# Revit family: ON2.5UM-NRG_5BF
name_source: partatom
category: Mechanical Equipment
units: mm (PartAtom-declared; Revit-internal decimal feet)

## family parameters
Always vertical = Yes
Cut with Voids When Loaded = No
OmniClass Number = 23.40.40.11.17
OmniClass Title = Refrigerated Cases
Part Type = Normal
Room Calculation Point = No
Round Connector Dimension = Use Radius
Shared = No
Work Plane-Based = Yes

## types (32) — shared parameters
11" BF = Yes
ANTI SWEAT HEATER AMPS = 0 A
BASE HEIGHT = 5 1/8"
BTU PER FOOT CONVENTIONAL = 797
BTU PER FOOT PARALLEL = 739
CERTIFICATIONS = NSF 7, UL471, CSA
COIL REFRIGERATION CHARGE = 0.00 lb
CONTROL TYPE = T-STAT
DATE = 10/03/12
DEDICATED CIRCUIT = YES
DEFROST PHASE = 1
DEFROST TIME AND DURATION = 2 @ 60 MIN
DEFROST WATTAGE = 0 W
DIEBOARD HEIGHT = 0"
DISCHARGE AIR TEMPERATURE = 28 °F
DRAIN LINE CONNECTION = Drain Connection
DRAIN LINE DIAMETER = 2"
DRAIN LINE RADIUS = 1"
DRAIN PIPE TYPE = PVC
DRIP PAN PLUMB TYPE = HARD
Default Elevation = 48"
Description = NARROW MULTI DECK MERCHANDISER
Discharge Air Velocity (FPM) = 250 FPM
ELECTRIC DEFROST = No
ELECTRICAL DEFROST VOLTAGE = 0 V
EVAPORATOR TEMPERATURE = 22 °F
FAN AMPS = 0 A
FAN CONNECTOR DESCRIPTION = FAN AND ANTI SWEAT CONNECTOR
FAN NUMBER OF POLES = 1
FAN TYPE = ECM
GROUND FAULT PROTECTION = NO
HOT GAS DEFROST = No
High Efficiency Amps = 0 A
High Power (Cornice) Amps = 0 A
ISOLATED GROUND REQUIRED = NO
Keynote = DAIRY/DELI/MEAT/PRODUCE/SEAFOOD
LED LIGHTING AMPS PER ROW = 0 A
LEGEND NUMBER = ON2.5UM-NRG
LIGHT TYPE = T8 FLUORESCENT
LIGHTING CONNECTION DESCRIPTION = LIGHTING CONNECTOR
LIGHTING NUMBER OF POLES = 1
LIQUID LINE CONNECTION = LIQUID LINE CONNECTION
LIQUID LINE DIAMETER = 0"
LIQUID LINE RADIUS = 0"
Manufacturer = HILL PHOENIX
Model = ON2.5UM-NRG
NUMBER OF WIRES = 3
PHASE = 1
POWER FACTOR = 1
PRESSURE REGULATOR = 0.00 psi
RECEPTICAL MOUNTING HEIGHT ABOVE FLOOR = 19 3/4"
REF PLANE FRONT BACK = 17 15/16"
REVERSE AIR DEFROST = No
SET BACK MODE FOR ENERGY CONSERVATION = NO
SHELVE 1 = Yes
SIZE OF COLD WATER HOOK UP = 0"
SIZE OF HOT WATER HOOK-UP = 0"
SUCTION LINE CONNECTION = SUCTION LINE CONNECTION
SUCTION LINE DIAMETER = 1"
SUCTION LINE RADIUS = 0"
Standard Power Amps = 0 A
Superheat Set Point @ Bulb (°F) = 6-8 °F
T8 LIGHT OR LED LIGHT = Yes
TIME OFF DEFROST = Yes
TOEKICK HEIGHT = 5 1/2"
TOEKICK INSET = 1 1/2"
URL = http://www.hillphoenix.com
VOLTAGE = 120 V
WATER LINE MOUNTING HEIGHT ABOVE FLOOR = 0"
WEIGHT = 0.00 lb
WIDTH = 35 13/16"
zero-valued in all types: CORNICE AND NOSE LIGHT ROWS

## per-type parameters (varying)
- ON2.5UM-12': 5" BF=Yes; ANTI SWEAT APPARENT LOAD=24 VA; ANTI SWEAT HEATER WATTAGE=24 W; BTU ADD FOR LIGHTS=720; BTU ADD PER SHELF PER FOOT=60; BTUH Conventional=0; BTUH Parallel=0; CONVENTIONAL EVAPORATOR LOAD=5502; DEFROST AMPS=3 A; DRAIN PIPE LENGTH=0"; Defrosts Per Day=0; Discharge Air (°F)=-460 °F; Evaporator (°F)=-460 °F; FAN AND ANTI SWEAT HEATER APPARENT LOAD=42 VA; FAN APPARENT LOAD=18 VA; FAN QUANTITY=2; FAN WATTAGE=9 W; HEIGHT=44 1/8"; High Efficiency Watts=11 W; High Power (Cornice) Watts=0 W; LED LIGHTING AMPS=0 A; LED LIGHTING BTU ADD PER ROW=27; LED LIGHTING WATTAGE=34 W; LENGTH=72"; LENGTH FOR BTU=6; LIGHT AMPS=1 A; LIGHTING APPARENT LOAD=89 VA; LIGHTING WATTAGE=89 VA; Lights Per Row=0; Number of Fans=1; PARALLEL EVAPORATOR LOAD=5154; REF PIPE LENGTH=28 5/8"; REF PLANE LEFT RIGHT=36"; SHELF LIGHT ROWS=2; SHELVE 2=No; SHELVE 3=Yes; SHELVE LENGTH=36"; Standard Power Watts=0 W; T8 LIGHTING AMPS=1 A; T8 LIGHTING AMPS PER ROW=0 A; T8 LIGHTING BTU ADD PER ROW=60; T8 LIGHTING WATTAGE=89 W; TOTAL APPARENT FAN-LIGHT AND A/S LOAD=122 VA; TOTAL CASE AMPS=1 A; TOTAL CASE WATTAGE=122 W; Timed-Off Defrost Termination Temp=-460 °F
- ON2.5UM-08': 5" BF=Yes; ANTI SWEAT APPARENT LOAD=30 VA; ANTI SWEAT HEATER WATTAGE=30 W; BTU ADD FOR LIGHTS=1280; BTU ADD PER SHELF PER FOOT=80; BTUH Conventional=715; BTUH Parallel=658; CONVENTIONAL EVAPORATOR LOAD=7656; DEFROST AMPS=4 A; DRAIN PIPE LENGTH=0"; Defrosts Per Day=6; Discharge Air (°F)=30 °F; Evaporator (°F)=26 °F; FAN AND ANTI SWEAT HEATER APPARENT LOAD=58 VA; FAN APPARENT LOAD=28 VA; FAN QUANTITY=3; FAN WATTAGE=14 W; HEIGHT=44 1/16"; High Efficiency Watts=22 W; High Power (Cornice) Watts=0 W; LED LIGHTING AMPS=0 A; LED LIGHTING BTU ADD PER ROW=36; LED LIGHTING WATTAGE=48 W; LENGTH=96"; LENGTH FOR BTU=8; LIGHT AMPS=1 A; LIGHTING APPARENT LOAD=113 VA; LIGHTING WATTAGE=113 VA; Lights Per Row=0; Number of Fans=2; PARALLEL EVAPORATOR LOAD=7192; REF PIPE LENGTH=28 5/8"; REF PLANE LEFT RIGHT=48"; SHELF LIGHT ROWS=2; SHELVE 2=No; SHELVE 3=Yes; SHELVE LENGTH=48"; Standard Power Watts=0 W; T8 LIGHTING AMPS=1 A; T8 LIGHTING AMPS PER ROW=0 A; T8 LIGHTING BTU ADD PER ROW=80; T8 LIGHTING WATTAGE=113 W; TOTAL APPARENT FAN-LIGHT AND A/S LOAD=157 VA; TOTAL CASE AMPS=1 A; TOTAL CASE WATTAGE=157 W; Timed-Off Defrost Fail-Safe (Min)=45; Timed-Off Defrost Termination Temp=42 °F
- ON2.5UM-06': 5" BF=Yes; ANTI SWEAT APPARENT LOAD=24 VA; ANTI SWEAT HEATER WATTAGE=24 W; BTU ADD FOR LIGHTS=720; BTU ADD PER SHELF PER FOOT=60; BTUH Conventional=0; BTUH Parallel=0; CONVENTIONAL EVAPORATOR LOAD=5502; DEFROST AMPS=3 A; DRAIN PIPE LENGTH=0"; Defrosts Per Day=0; Discharge Air (°F)=-460 °F; Evaporator (°F)=-460 °F; FAN AND ANTI SWEAT HEATER APPARENT LOAD=42 VA; FAN APPARENT LOAD=18 VA; FAN QUANTITY=2; FAN WATTAGE=9 W; HEIGHT=44 1/16"; High Efficiency Watts=11 W; High Power (Cornice) Watts=0 W; LED LIGHTING AMPS=0 A; LED LIGHTING BTU ADD PER ROW=27; LED LIGHTING WATTAGE=34 W; LENGTH=72"; LENGTH FOR BTU=6; LIGHT AMPS=1 A; LIGHTING APPARENT LOAD=89 VA; LIGHTING WATTAGE=89 VA; Lights Per Row=0; Number of Fans=1; PARALLEL EVAPORATOR LOAD=5154; REF PIPE LENGTH=28 5/8"; REF PLANE LEFT RIGHT=36"; SHELF LIGHT ROWS=2; SHELVE 2=No; SHELVE 3=Yes; SHELVE LENGTH=36"; Standard Power Watts=0 W; T8 LIGHTING AMPS=1 A; T8 LIGHTING AMPS PER ROW=0 A; T8 LIGHTING BTU ADD PER ROW=60; T8 LIGHTING WATTAGE=89 W; TOTAL APPARENT FAN-LIGHT AND A/S LOAD=122 VA; TOTAL CASE AMPS=1 A; TOTAL CASE WATTAGE=122 W; Timed-Off Defrost Termination Temp=-460 °F
- ON2.5UM-04': 5" BF=No; ANTI SWEAT APPARENT LOAD=17 VA; ANTI SWEAT HEATER WATTAGE=17 W; BTU ADD FOR LIGHTS=320; BTU ADD PER SHELF PER FOOT=80; BTUH Conventional=0; BTUH Parallel=0; CONVENTIONAL EVAPORATOR LOAD=3508; DEFROST AMPS=2 A; DRAIN PIPE LENGTH=12"; Defrosts Per Day=6; Discharge Air (°F)=-460 °F; Evaporator (°F)=-460 °F; FAN AND ANTI SWEAT HEATER APPARENT LOAD=35 VA; FAN APPARENT LOAD=18 VA; FAN QUANTITY=2; FAN WATTAGE=9 W; HEIGHT=44 1/16"; High Efficiency Watts=11 W; High Power (Cornice) Watts=15 W; LED LIGHTING AMPS=0 A; LED LIGHTING BTU ADD PER ROW=36; LED LIGHTING WATTAGE=12 W; LENGTH=48"; LENGTH FOR BTU=4; LIGHT AMPS=0 A; LIGHTING APPARENT LOAD=28 VA; LIGHTING WATTAGE=28 VA; Light Length=4'; Lights Per Row=1; Number of Fans=1; PARALLEL EVAPORATOR LOAD=3276; REF PIPE LENGTH=22 9/16"; REF PLANE LEFT RIGHT=24"; SHELF LIGHT ROWS=1; SHELVE 2=No; SHELVE 3=No; SHELVE LENGTH=48"; Standard Power Watts=6 W; T8 LIGHTING AMPS=0 A; T8 LIGHTING AMPS PER ROW=0 A; T8 LIGHTING BTU ADD PER ROW=80; T8 LIGHTING WATTAGE=28 W; TOTAL APPARENT FAN-LIGHT AND A/S LOAD=54 VA; TOTAL CASE AMPS=1 A; TOTAL CASE WATTAGE=54 W; Timed-Off Defrost Fail-Safe (Min)=45; Timed-Off Defrost Termination Temp=42 °F
- ON2.5UM-04' - Dairy/Deli: 5" BF=No; ANTI SWEAT APPARENT LOAD=17 VA; ANTI SWEAT HEATER WATTAGE=17 W; BTU ADD FOR LIGHTS=320; BTU ADD PER SHELF PER FOOT=80; BTUH Conventional=0; BTUH Parallel=0; CONVENTIONAL EVAPORATOR LOAD=3508; DEFROST AMPS=2 A; DRAIN PIPE LENGTH=12"; Defrosts Per Day=6; Discharge Air (°F)=-460 °F; Evaporator (°F)=-460 °F; FAN AND ANTI SWEAT HEATER APPARENT LOAD=35 VA; FAN APPARENT LOAD=18 VA; FAN QUANTITY=2; FAN WATTAGE=9 W; HEIGHT=44 1/16"; High Efficiency Watts=11 W; High Power (Cornice) Watts=15 W; LED LIGHTING AMPS=0 A; LED LIGHTING BTU ADD PER ROW=36; LED LIGHTING WATTAGE=12 W; LENGTH=48"; LENGTH FOR BTU=4; LIGHT AMPS=0 A; LIGHTING APPARENT LOAD=28 VA; LIGHTING WATTAGE=28 VA; Light Length=4'; Lights Per Row=1; Number of Fans=1; PARALLEL EVAPORATOR LOAD=3276; REF PIPE LENGTH=22 9/16"; REF PLANE LEFT RIGHT=24"; SHELF LIGHT ROWS=1; SHELVE 2=No; SHELVE 3=No; SHELVE LENGTH=48"; Standard Power Watts=6 W; T8 LIGHTING AMPS=0 A; T8 LIGHTING AMPS PER ROW=0 A; T8 LIGHTING BTU ADD PER ROW=80; T8 LIGHTING WATTAGE=28 W; TOTAL APPARENT FAN-LIGHT AND A/S LOAD=54 VA; TOTAL CASE AMPS=1 A; TOTAL CASE WATTAGE=54 W; Timed-Off Defrost Fail-Safe (Min)=45; Timed-Off Defrost Termination Temp=42 °F
- ON2.5UM-04' - Cut Produce: 5" BF=No; ANTI SWEAT APPARENT LOAD=17 VA; ANTI SWEAT HEATER WATTAGE=17 W; BTU ADD FOR LIGHTS=320; BTU ADD PER SHELF PER FOOT=80; BTUH Conventional=0; BTUH Parallel=0; CONVENTIONAL EVAPORATOR LOAD=3508; DEFROST AMPS=2 A; DRAIN PIPE LENGTH=12"; Defrosts Per Day=6; Discharge Air (°F)=-460 °F; Evaporator (°F)=-460 °F; FAN AND ANTI SWEAT HEATER APPARENT LOAD=35 VA; FAN APPARENT LOAD=18 VA; FAN QUANTITY=2; FAN WATTAGE=9 W; HEIGHT=44 1/16"; High Efficiency Watts=11 W; High Power (Cornice) Watts=15 W; LED LIGHTING AMPS=0 A; LED LIGHTING BTU ADD PER ROW=36; LED LIGHTING WATTAGE=12 W; LENGTH=48"; LENGTH FOR BTU=4; LIGHT AMPS=0 A; LIGHTING APPARENT LOAD=28 VA; LIGHTING WATTAGE=28 VA; Light Length=4'; Lights Per Row=1; Number of Fans=1; PARALLEL EVAPORATOR LOAD=3276; REF PIPE LENGTH=22 9/16"; REF PLANE LEFT RIGHT=24"; SHELF LIGHT ROWS=1; SHELVE 2=No; SHELVE 3=No; SHELVE LENGTH=48"; Standard Power Watts=6 W; T8 LIGHTING AMPS=0 A; T8 LIGHTING AMPS PER ROW=0 A; T8 LIGHTING BTU ADD PER ROW=80; T8 LIGHTING WATTAGE=28 W; TOTAL APPARENT FAN-LIGHT AND A/S LOAD=54 VA; TOTAL CASE AMPS=1 A; TOTAL CASE WATTAGE=54 W; Timed-Off Defrost Fail-Safe (Min)=45; Timed-Off Defrost Termination Temp=42 °F
- ON2.5UM-04' - Cut Produce - Extended: 5" BF=No; ANTI SWEAT APPARENT LOAD=17 VA; ANTI SWEAT HEATER WATTAGE=17 W; BTU ADD FOR LIGHTS=320; BTU ADD PER SHELF PER FOOT=80; BTUH Conventional=0; BTUH Parallel=0; CONVENTIONAL EVAPORATOR LOAD=3508; DEFROST AMPS=2 A; DRAIN PIPE LENGTH=12"; Defrosts Per Day=6; Discharge Air (°F)=-460 °F; Evaporator (°F)=-460 °F; FAN AND ANTI SWEAT HEATER APPARENT LOAD=35 VA; FAN APPARENT LOAD=18 VA; FAN QUANTITY=2; FAN WATTAGE=9 W; HEIGHT=44 1/16"; High Efficiency Watts=11 W; High Power (Cornice) Watts=15 W; LED LIGHTING AMPS=0 A; LED LIGHTING BTU ADD PER ROW=36; LED LIGHTING WATTAGE=12 W; LENGTH=48"; LENGTH FOR BTU=4; LIGHT AMPS=0 A; LIGHTING APPARENT LOAD=28 VA; LIGHTING WATTAGE=28 VA; Light Length=4'; Lights Per Row=1; Number of Fans=1; PARALLEL EVAPORATOR LOAD=3276; REF PIPE LENGTH=22 9/16"; REF PLANE LEFT RIGHT=24"; SHELF LIGHT ROWS=1; SHELVE 2=No; SHELVE 3=No; SHELVE LENGTH=48"; Standard Power Watts=6 W; T8 LIGHTING AMPS=0 A; T8 LIGHTING AMPS PER ROW=0 A; T8 LIGHTING BTU ADD PER ROW=80; T8 LIGHTING WATTAGE=28 W; TOTAL APPARENT FAN-LIGHT AND A/S LOAD=54 VA; TOTAL CASE AMPS=1 A; TOTAL CASE WATTAGE=54 W; Timed-Off Defrost Fail-Safe (Min)=45; Timed-Off Defrost Termination Temp=42 °F
- ON2.5UM-04' - Meat: 5" BF=No; ANTI SWEAT APPARENT LOAD=17 VA; ANTI SWEAT HEATER WATTAGE=17 W; BTU ADD FOR LIGHTS=320; BTU ADD PER SHELF PER FOOT=80; BTUH Conventional=0; BTUH Parallel=0; CONVENTIONAL EVAPORATOR LOAD=3508; DEFROST AMPS=2 A; DRAIN PIPE LENGTH=12"; Defrosts Per Day=6; Discharge Air (°F)=-460 °F; Evaporator (°F)=-460 °F; FAN AND ANTI SWEAT HEATER APPARENT LOAD=35 VA; FAN APPARENT LOAD=18 VA; FAN QUANTITY=2; FAN WATTAGE=9 W; HEIGHT=44 1/16"; High Efficiency Watts=11 W; High Power (Cornice) Watts=15 W; LED LIGHTING AMPS=0 A; LED LIGHTING BTU ADD PER ROW=36; LED LIGHTING WATTAGE=12 W; LENGTH=48"; LENGTH FOR BTU=4; LIGHT AMPS=0 A; LIGHTING APPARENT LOAD=28 VA; LIGHTING WATTAGE=28 VA; Light Length=4'; Lights Per Row=1; Number of Fans=1; PARALLEL EVAPORATOR LOAD=3276; REF PIPE LENGTH=22 9/16"; REF PLANE LEFT RIGHT=24"; SHELF LIGHT ROWS=1; SHELVE 2=No; SHELVE 3=No; SHELVE LENGTH=48"; Standard Power Watts=6 W; T8 LIGHTING AMPS=0 A; T8 LIGHTING AMPS PER ROW=0 A; T8 LIGHTING BTU ADD PER ROW=80; T8 LIGHTING WATTAGE=28 W; TOTAL APPARENT FAN-LIGHT AND A/S LOAD=54 VA; TOTAL CASE AMPS=1 A; TOTAL CASE WATTAGE=54 W; Timed-Off Defrost Fail-Safe (Min)=45; Timed-Off Defrost Termination Temp=42 °F
- ON2.5UM-04' - Meat - Extended: 5" BF=No; ANTI SWEAT APPARENT LOAD=17 VA; ANTI SWEAT HEATER WATTAGE=17 W; BTU ADD FOR LIGHTS=320; BTU ADD PER SHELF PER FOOT=80; BTUH Conventional=0; BTUH Parallel=0; CONVENTIONAL EVAPORATOR LOAD=3508; DEFROST AMPS=2 A; DRAIN PIPE LENGTH=12"; Defrosts Per Day=6; Discharge Air (°F)=-460 °F; Evaporator (°F)=-460 °F; FAN AND ANTI SWEAT HEATER APPARENT LOAD=35 VA; FAN APPARENT LOAD=18 VA; FAN QUANTITY=2; FAN WATTAGE=9 W; HEIGHT=44 1/16"; High Efficiency Watts=11 W; High Power (Cornice) Watts=15 W; LED LIGHTING AMPS=0 A; LED LIGHTING BTU ADD PER ROW=36; LED LIGHTING WATTAGE=12 W; LENGTH=48"; LENGTH FOR BTU=4; LIGHT AMPS=0 A; LIGHTING APPARENT LOAD=28 VA; LIGHTING WATTAGE=28 VA; Light Length=4'; Lights Per Row=1; Number of Fans=1; PARALLEL EVAPORATOR LOAD=3276; REF PIPE LENGTH=22 9/16"; REF PLANE LEFT RIGHT=24"; SHELF LIGHT ROWS=1; SHELVE 2=No; SHELVE 3=No; SHELVE LENGTH=48"; Standard Power Watts=6 W; T8 LIGHTING AMPS=0 A; T8 LIGHTING AMPS PER ROW=0 A; T8 LIGHTING BTU ADD PER ROW=80; T8 LIGHTING WATTAGE=28 W; TOTAL APPARENT FAN-LIGHT AND A/S LOAD=54 VA; TOTAL CASE AMPS=1 A; TOTAL CASE WATTAGE=54 W; Timed-Off Defrost Fail-Safe (Min)=45; Timed-Off Defrost Termination Temp=42 °F
- ON2.5UM-04' - Dairy/Deli - Extended: 5" BF=No; ANTI SWEAT APPARENT LOAD=17 VA; ANTI SWEAT HEATER WATTAGE=17 W; BTU ADD FOR LIGHTS=320; BTU ADD PER SHELF PER FOOT=80; BTUH Conventional=0; BTUH Parallel=0; CONVENTIONAL EVAPORATOR LOAD=3508; DEFROST AMPS=2 A; DRAIN PIPE LENGTH=12"; Defrosts Per Day=6; Discharge Air (°F)=-460 °F; Evaporator (°F)=-460 °F; FAN AND ANTI SWEAT HEATER APPARENT LOAD=35 VA; FAN APPARENT LOAD=18 VA; FAN QUANTITY=2; FAN WATTAGE=9 W; HEIGHT=44 1/16"; High Efficiency Watts=11 W; High Power (Cornice) Watts=15 W; LED LIGHTING AMPS=0 A; LED LIGHTING BTU ADD PER ROW=36; LED LIGHTING WATTAGE=12 W; LENGTH=48"; LENGTH FOR BTU=4; LIGHT AMPS=0 A; LIGHTING APPARENT LOAD=28 VA; LIGHTING WATTAGE=28 VA; Light Length=4'; Lights Per Row=1; Number of Fans=1; PARALLEL EVAPORATOR LOAD=3276; REF PIPE LENGTH=22 9/16"; REF PLANE LEFT RIGHT=24"; SHELF LIGHT ROWS=1; SHELVE 2=No; SHELVE 3=No; SHELVE LENGTH=48"; Standard Power Watts=6 W; T8 LIGHTING AMPS=0 A; T8 LIGHTING AMPS PER ROW=0 A; T8 LIGHTING BTU ADD PER ROW=80; T8 LIGHTING WATTAGE=28 W; TOTAL APPARENT FAN-LIGHT AND A/S LOAD=54 VA; TOTAL CASE AMPS=1 A; TOTAL CASE WATTAGE=54 W; Timed-Off Defrost Fail-Safe (Min)=45; Timed-Off Defrost Termination Temp=42 °F
- ON2.5UM-06' Dairy/Produce - Extended: 5" BF=Yes; ANTI SWEAT APPARENT LOAD=24 VA; ANTI SWEAT HEATER WATTAGE=24 W; BTU ADD FOR LIGHTS=720; BTU ADD PER SHELF PER FOOT=60; BTUH Conventional=0; BTUH Parallel=0; CONVENTIONAL EVAPORATOR LOAD=5502; DEFROST AMPS=3 A; DRAIN PIPE LENGTH=0"; Defrosts Per Day=0; Discharge Air (°F)=-460 °F; Evaporator (°F)=-460 °F; FAN AND ANTI SWEAT HEATER APPARENT LOAD=42 VA; FAN APPARENT LOAD=18 VA; FAN QUANTITY=2; FAN WATTAGE=9 W; HEIGHT=44 1/16"; High Efficiency Watts=11 W; High Power (Cornice) Watts=0 W; LED LIGHTING AMPS=0 A; LED LIGHTING BTU ADD PER ROW=27; LED LIGHTING WATTAGE=34 W; LENGTH=72"; LENGTH FOR BTU=6; LIGHT AMPS=1 A; LIGHTING APPARENT LOAD=89 VA; LIGHTING WATTAGE=89 VA; Lights Per Row=0; Number of Fans=1; PARALLEL EVAPORATOR LOAD=5154; REF PIPE LENGTH=28 5/8"; REF PLANE LEFT RIGHT=36"; SHELF LIGHT ROWS=2; SHELVE 2=No; SHELVE 3=Yes; SHELVE LENGTH=36"; Standard Power Watts=0 W; T8 LIGHTING AMPS=1 A; T8 LIGHTING AMPS PER ROW=0 A; T8 LIGHTING BTU ADD PER ROW=60; T8 LIGHTING WATTAGE=89 W; TOTAL APPARENT FAN-LIGHT AND A/S LOAD=122 VA; TOTAL CASE AMPS=1 A; TOTAL CASE WATTAGE=122 W; Timed-Off Defrost Termination Temp=-460 °F
- ON2.5UM-08' Dairy/Produce - Extended: 5" BF=Yes; ANTI SWEAT APPARENT LOAD=30 VA; ANTI SWEAT HEATER WATTAGE=30 W; BTU ADD FOR LIGHTS=1280; BTU ADD PER SHELF PER FOOT=80; BTUH Conventional=715; BTUH Parallel=658; CONVENTIONAL EVAPORATOR LOAD=7656; DEFROST AMPS=4 A; DRAIN PIPE LENGTH=0"; Defrosts Per Day=6; Discharge Air (°F)=30 °F; Evaporator (°F)=26 °F; FAN AND ANTI SWEAT HEATER APPARENT LOAD=58 VA; FAN APPARENT LOAD=28 VA; FAN QUANTITY=3; FAN WATTAGE=14 W; HEIGHT=44 1/16"; High Efficiency Watts=22 W; High Power (Cornice) Watts=0 W; LED LIGHTING AMPS=0 A; LED LIGHTING BTU ADD PER ROW=36; LED LIGHTING WATTAGE=48 W; LENGTH=96"; LENGTH FOR BTU=8; LIGHT AMPS=1 A; LIGHTING APPARENT LOAD=113 VA; LIGHTING WATTAGE=113 VA; Lights Per Row=0; Number of Fans=2; PARALLEL EVAPORATOR LOAD=7192; REF PIPE LENGTH=28 5/8"; REF PLANE LEFT RIGHT=48"; SHELF LIGHT ROWS=2; SHELVE 2=No; SHELVE 3=Yes; SHELVE LENGTH=48"; Standard Power Watts=0 W; T8 LIGHTING AMPS=1 A; T8 LIGHTING AMPS PER ROW=0 A; T8 LIGHTING BTU ADD PER ROW=80; T8 LIGHTING WATTAGE=113 W; TOTAL APPARENT FAN-LIGHT AND A/S LOAD=157 VA; TOTAL CASE AMPS=1 A; TOTAL CASE WATTAGE=157 W; Timed-Off Defrost Fail-Safe (Min)=45; Timed-Off Defrost Termination Temp=42 °F
- ON2.5UM-12' Dairy/Produce - Extended: 5" BF=Yes; ANTI SWEAT APPARENT LOAD=46 VA; ANTI SWEAT HEATER WATTAGE=46 W; BTU ADD FOR LIGHTS=2880; BTU ADD PER SHELF PER FOOT=80; BTUH Conventional=0; BTUH Parallel=0; CONVENTIONAL EVAPORATOR LOAD=12444; DEFROST AMPS=6 A; DRAIN PIPE LENGTH=0"; Defrosts Per Day=0; Discharge Air (°F)=-460 °F; Evaporator (°F)=-460 °F; FAN AND ANTI SWEAT HEATER APPARENT LOAD=83 VA; FAN APPARENT LOAD=37 VA; FAN QUANTITY=4; FAN WATTAGE=18 W; HEIGHT=44 1/16"; High Efficiency Watts=11 W; High Power (Cornice) Watts=0 W; LED LIGHTING AMPS=1 A; LED LIGHTING BTU ADD PER ROW=36; LED LIGHTING WATTAGE=108 W; LENGTH=144"; LENGTH FOR BTU=12; LIGHT AMPS=2 A; LIGHTING APPARENT LOAD=252 VA; LIGHTING WATTAGE=252 VA; Lights Per Row=0; Number of Fans=1; PARALLEL EVAPORATOR LOAD=11748; REF PIPE LENGTH=28 5/8"; REF PLANE LEFT RIGHT=72"; SHELF LIGHT ROWS=3; SHELVE 2=Yes; SHELVE 3=Yes; SHELVE LENGTH=48"; Standard Power Watts=0 W; T8 LIGHTING AMPS=2 A; T8 LIGHTING AMPS PER ROW=1 A; T8 LIGHTING BTU ADD PER ROW=80; T8 LIGHTING WATTAGE=252 W; TOTAL APPARENT FAN-LIGHT AND A/S LOAD=316 VA; TOTAL CASE AMPS=3 A; TOTAL CASE WATTAGE=316 W; Timed-Off Defrost Termination Temp=-460 °F
- ON2.5UM-06' Dairy/Produce: 5" BF=Yes; ANTI SWEAT APPARENT LOAD=24 VA; ANTI SWEAT HEATER WATTAGE=24 W; BTU ADD FOR LIGHTS=720; BTU ADD PER SHELF PER FOOT=60; BTUH Conventional=0; BTUH Parallel=0; CONVENTIONAL EVAPORATOR LOAD=5502; DEFROST AMPS=3 A; DRAIN PIPE LENGTH=0"; Defrosts Per Day=0; Discharge Air (°F)=-460 °F; Evaporator (°F)=-460 °F; FAN AND ANTI SWEAT HEATER APPARENT LOAD=42 VA; FAN APPARENT LOAD=18 VA; FAN QUANTITY=2; FAN WATTAGE=9 W; HEIGHT=44 1/16"; High Efficiency Watts=11 W; High Power (Cornice) Watts=0 W; LED LIGHTING AMPS=0 A; LED LIGHTING BTU ADD PER ROW=27; LED LIGHTING WATTAGE=34 W; LENGTH=72"; LENGTH FOR BTU=6; LIGHT AMPS=1 A; LIGHTING APPARENT LOAD=89 VA; LIGHTING WATTAGE=89 VA; Lights Per Row=0; Number of Fans=1; PARALLEL EVAPORATOR LOAD=5154; REF PIPE LENGTH=28 5/8"; REF PLANE LEFT RIGHT=36"; SHELF LIGHT ROWS=2; SHELVE 2=No; SHELVE 3=Yes; SHELVE LENGTH=36"; Standard Power Watts=0 W; T8 LIGHTING AMPS=1 A; T8 LIGHTING AMPS PER ROW=0 A; T8 LIGHTING BTU ADD PER ROW=60; T8 LIGHTING WATTAGE=89 W; TOTAL APPARENT FAN-LIGHT AND A/S LOAD=122 VA; TOTAL CASE AMPS=1 A; TOTAL CASE WATTAGE=122 W; Timed-Off Defrost Termination Temp=-460 °F
- ON2.5UM-08' Dairy/Produce: 5" BF=Yes; ANTI SWEAT APPARENT LOAD=30 VA; ANTI SWEAT HEATER WATTAGE=30 W; BTU ADD FOR LIGHTS=1280; BTU ADD PER SHELF PER FOOT=80; BTUH Conventional=715; BTUH Parallel=658; CONVENTIONAL EVAPORATOR LOAD=7656; DEFROST AMPS=4 A; DRAIN PIPE LENGTH=0"; Defrosts Per Day=6; Discharge Air (°F)=30 °F; Evaporator (°F)=26 °F; FAN AND ANTI SWEAT HEATER APPARENT LOAD=58 VA; FAN APPARENT LOAD=28 VA; FAN QUANTITY=3; FAN WATTAGE=14 W; HEIGHT=44 1/16"; High Efficiency Watts=22 W; High Power (Cornice) Watts=0 W; LED LIGHTING AMPS=0 A; LED LIGHTING BTU ADD PER ROW=36; LED LIGHTING WATTAGE=48 W; LENGTH=96"; LENGTH FOR BTU=8; LIGHT AMPS=1 A; LIGHTING APPARENT LOAD=113 VA; LIGHTING WATTAGE=113 VA; Lights Per Row=0; Number of Fans=2; PARALLEL EVAPORATOR LOAD=7192; REF PIPE LENGTH=28 5/8"; REF PLANE LEFT RIGHT=48"; SHELF LIGHT ROWS=2; SHELVE 2=No; SHELVE 3=Yes; SHELVE LENGTH=48"; Standard Power Watts=0 W; T8 LIGHTING AMPS=1 A; T8 LIGHTING AMPS PER ROW=0 A; T8 LIGHTING BTU ADD PER ROW=80; T8 LIGHTING WATTAGE=113 W; TOTAL APPARENT FAN-LIGHT AND A/S LOAD=157 VA; TOTAL CASE AMPS=1 A; TOTAL CASE WATTAGE=157 W; Timed-Off Defrost Fail-Safe (Min)=45; Timed-Off Defrost Termination Temp=42 °F
- ON2.5UM-12' Dairy/Produce: 5" BF=Yes; ANTI SWEAT APPARENT LOAD=46 VA; ANTI SWEAT HEATER WATTAGE=46 W; BTU ADD FOR LIGHTS=2880; BTU ADD PER SHELF PER FOOT=80; BTUH Conventional=0; BTUH Parallel=0; CONVENTIONAL EVAPORATOR LOAD=12444; DEFROST AMPS=6 A; DRAIN PIPE LENGTH=0"; Defrosts Per Day=0; Discharge Air (°F)=-460 °F; Evaporator (°F)=-460 °F; FAN AND ANTI SWEAT HEATER APPARENT LOAD=83 VA; FAN APPARENT LOAD=37 VA; FAN QUANTITY=4; FAN WATTAGE=18 W; HEIGHT=44 1/16"; High Efficiency Watts=11 W; High Power (Cornice) Watts=0 W; LED LIGHTING AMPS=1 A; LED LIGHTING BTU ADD PER ROW=36; LED LIGHTING WATTAGE=108 W; LENGTH=144"; LENGTH FOR BTU=12; LIGHT AMPS=2 A; LIGHTING APPARENT LOAD=252 VA; LIGHTING WATTAGE=252 VA; Lights Per Row=0; Number of Fans=1; PARALLEL EVAPORATOR LOAD=11748; REF PIPE LENGTH=28 5/8"; REF PLANE LEFT RIGHT=72"; SHELF LIGHT ROWS=3; SHELVE 2=Yes; SHELVE 3=Yes; SHELVE LENGTH=48"; Standard Power Watts=0 W; T8 LIGHTING AMPS=2 A; T8 LIGHTING AMPS PER ROW=1 A; T8 LIGHTING BTU ADD PER ROW=80; T8 LIGHTING WATTAGE=252 W; TOTAL APPARENT FAN-LIGHT AND A/S LOAD=316 VA; TOTAL CASE AMPS=3 A; TOTAL CASE WATTAGE=316 W; Timed-Off Defrost Termination Temp=-460 °F
- ON2.5UM-08' Cut Produce: 5" BF=Yes; ANTI SWEAT APPARENT LOAD=24 VA; ANTI SWEAT HEATER WATTAGE=24 W; BTU ADD FOR LIGHTS=720; BTU ADD PER SHELF PER FOOT=60; BTUH Conventional=0; BTUH Parallel=0; CONVENTIONAL EVAPORATOR LOAD=5502; DEFROST AMPS=3 A; DRAIN PIPE LENGTH=0"; Defrosts Per Day=0; Discharge Air (°F)=-460 °F; Evaporator (°F)=-460 °F; FAN AND ANTI SWEAT HEATER APPARENT LOAD=42 VA; FAN APPARENT LOAD=18 VA; FAN QUANTITY=2; FAN WATTAGE=9 W; HEIGHT=44 1/16"; High Efficiency Watts=11 W; High Power (Cornice) Watts=0 W; LED LIGHTING AMPS=0 A; LED LIGHTING BTU ADD PER ROW=27; LED LIGHTING WATTAGE=34 W; LENGTH=72"; LENGTH FOR BTU=6; LIGHT AMPS=1 A; LIGHTING APPARENT LOAD=89 VA; LIGHTING WATTAGE=89 VA; Lights Per Row=0; Number of Fans=1; PARALLEL EVAPORATOR LOAD=5154; REF PIPE LENGTH=28 5/8"; REF PLANE LEFT RIGHT=36"; SHELF LIGHT ROWS=2; SHELVE 2=No; SHELVE 3=Yes; SHELVE LENGTH=36"; Standard Power Watts=0 W; T8 LIGHTING AMPS=1 A; T8 LIGHTING AMPS PER ROW=0 A; T8 LIGHTING BTU ADD PER ROW=60; T8 LIGHTING WATTAGE=89 W; TOTAL APPARENT FAN-LIGHT AND A/S LOAD=122 VA; TOTAL CASE AMPS=1 A; TOTAL CASE WATTAGE=122 W; Timed-Off Defrost Termination Temp=-460 °F
- ON2.5UM-06' Cut Produce: 5" BF=Yes; ANTI SWEAT APPARENT LOAD=24 VA; ANTI SWEAT HEATER WATTAGE=24 W; BTU ADD FOR LIGHTS=720; BTU ADD PER SHELF PER FOOT=60; BTUH Conventional=0; BTUH Parallel=0; CONVENTIONAL EVAPORATOR LOAD=5502; DEFROST AMPS=3 A; DRAIN PIPE LENGTH=0"; Defrosts Per Day=0; Discharge Air (°F)=-460 °F; Evaporator (°F)=-460 °F; FAN AND ANTI SWEAT HEATER APPARENT LOAD=42 VA; FAN APPARENT LOAD=18 VA; FAN QUANTITY=2; FAN WATTAGE=9 W; HEIGHT=44 1/16"; High Efficiency Watts=11 W; High Power (Cornice) Watts=0 W; LED LIGHTING AMPS=0 A; LED LIGHTING BTU ADD PER ROW=27; LED LIGHTING WATTAGE=34 W; LENGTH=72"; LENGTH FOR BTU=6; LIGHT AMPS=1 A; LIGHTING APPARENT LOAD=89 VA; LIGHTING WATTAGE=89 VA; Lights Per Row=0; Number of Fans=1; PARALLEL EVAPORATOR LOAD=5154; REF PIPE LENGTH=28 5/8"; REF PLANE LEFT RIGHT=36"; SHELF LIGHT ROWS=2; SHELVE 2=No; SHELVE 3=Yes; SHELVE LENGTH=36"; Standard Power Watts=0 W; T8 LIGHTING AMPS=1 A; T8 LIGHTING AMPS PER ROW=0 A; T8 LIGHTING BTU ADD PER ROW=60; T8 LIGHTING WATTAGE=89 W; TOTAL APPARENT FAN-LIGHT AND A/S LOAD=122 VA; TOTAL CASE AMPS=1 A; TOTAL CASE WATTAGE=122 W; Timed-Off Defrost Termination Temp=-460 °F
- ON2.5UM-12' Cut Produce: 5" BF=Yes; ANTI SWEAT APPARENT LOAD=46 VA; ANTI SWEAT HEATER WATTAGE=46 W; BTU ADD FOR LIGHTS=2880; BTU ADD PER SHELF PER FOOT=80; BTUH Conventional=0; BTUH Parallel=0; CONVENTIONAL EVAPORATOR LOAD=12444; DEFROST AMPS=6 A; DRAIN PIPE LENGTH=0"; Defrosts Per Day=0; Discharge Air (°F)=-460 °F; Evaporator (°F)=-460 °F; FAN AND ANTI SWEAT HEATER APPARENT LOAD=83 VA; FAN APPARENT LOAD=37 VA; FAN QUANTITY=4; FAN WATTAGE=18 W; HEIGHT=44 1/16"; High Efficiency Watts=11 W; High Power (Cornice) Watts=0 W; LED LIGHTING AMPS=1 A; LED LIGHTING BTU ADD PER ROW=36; LED LIGHTING WATTAGE=108 W; LENGTH=144"; LENGTH FOR BTU=12; LIGHT AMPS=2 A; LIGHTING APPARENT LOAD=252 VA; LIGHTING WATTAGE=252 VA; Lights Per Row=0; Number of Fans=1; PARALLEL EVAPORATOR LOAD=11748; REF PIPE LENGTH=28 5/8"; REF PLANE LEFT RIGHT=72"; SHELF LIGHT ROWS=3; SHELVE 2=Yes; SHELVE 3=Yes; SHELVE LENGTH=48"; Standard Power Watts=0 W; T8 LIGHTING AMPS=2 A; T8 LIGHTING AMPS PER ROW=1 A; T8 LIGHTING BTU ADD PER ROW=80; T8 LIGHTING WATTAGE=252 W; TOTAL APPARENT FAN-LIGHT AND A/S LOAD=316 VA; TOTAL CASE AMPS=3 A; TOTAL CASE WATTAGE=316 W; Timed-Off Defrost Termination Temp=-460 °F
- ON2.5UM-12' Cut Produce - Extended: 5" BF=Yes; ANTI SWEAT APPARENT LOAD=46 VA; ANTI SWEAT HEATER WATTAGE=46 W; BTU ADD FOR LIGHTS=2880; BTU ADD PER SHELF PER FOOT=80; BTUH Conventional=0; BTUH Parallel=0; CONVENTIONAL EVAPORATOR LOAD=12444; DEFROST AMPS=6 A; DRAIN PIPE LENGTH=0"; Defrosts Per Day=0; Discharge Air (°F)=-460 °F; Evaporator (°F)=-460 °F; FAN AND ANTI SWEAT HEATER APPARENT LOAD=83 VA; FAN APPARENT LOAD=37 VA; FAN QUANTITY=4; FAN WATTAGE=18 W; HEIGHT=44 1/16"; High Efficiency Watts=11 W; High Power (Cornice) Watts=0 W; LED LIGHTING AMPS=1 A; LED LIGHTING BTU ADD PER ROW=36; LED LIGHTING WATTAGE=108 W; LENGTH=144"; LENGTH FOR BTU=12; LIGHT AMPS=2 A; LIGHTING APPARENT LOAD=252 VA; LIGHTING WATTAGE=252 VA; Lights Per Row=0; Number of Fans=1; PARALLEL EVAPORATOR LOAD=11748; REF PIPE LENGTH=28 5/8"; REF PLANE LEFT RIGHT=72"; SHELF LIGHT ROWS=3; SHELVE 2=Yes; SHELVE 3=Yes; SHELVE LENGTH=48"; Standard Power Watts=0 W; T8 LIGHTING AMPS=2 A; T8 LIGHTING AMPS PER ROW=1 A; T8 LIGHTING BTU ADD PER ROW=80; T8 LIGHTING WATTAGE=252 W; TOTAL APPARENT FAN-LIGHT AND A/S LOAD=316 VA; TOTAL CASE AMPS=3 A; TOTAL CASE WATTAGE=316 W; Timed-Off Defrost Termination Temp=-460 °F
- ON2.5UM-12' - Meat - Extended: 5" BF=Yes; ANTI SWEAT APPARENT LOAD=46 VA; ANTI SWEAT HEATER WATTAGE=46 W; BTU ADD FOR LIGHTS=2880; BTU ADD PER SHELF PER FOOT=80; BTUH Conventional=0; BTUH Parallel=0; CONVENTIONAL EVAPORATOR LOAD=12444; DEFROST AMPS=6 A; DRAIN PIPE LENGTH=0"; Defrosts Per Day=0; Discharge Air (°F)=-460 °F; Evaporator (°F)=-460 °F; FAN AND ANTI SWEAT HEATER APPARENT LOAD=83 VA; FAN APPARENT LOAD=37 VA; FAN QUANTITY=4; FAN WATTAGE=18 W; HEIGHT=44 1/16"; High Efficiency Watts=11 W; High Power (Cornice) Watts=0 W; LED LIGHTING AMPS=1 A; LED LIGHTING BTU ADD PER ROW=36; LED LIGHTING WATTAGE=108 W; LENGTH=144"; LENGTH FOR BTU=12; LIGHT AMPS=2 A; LIGHTING APPARENT LOAD=252 VA; LIGHTING WATTAGE=252 VA; Lights Per Row=0; Number of Fans=1; PARALLEL EVAPORATOR LOAD=11748; REF PIPE LENGTH=28 5/8"; REF PLANE LEFT RIGHT=72"; SHELF LIGHT ROWS=3; SHELVE 2=Yes; SHELVE 3=Yes; SHELVE LENGTH=48"; Standard Power Watts=0 W; T8 LIGHTING AMPS=2 A; T8 LIGHTING AMPS PER ROW=1 A; T8 LIGHTING BTU ADD PER ROW=80; T8 LIGHTING WATTAGE=252 W; TOTAL APPARENT FAN-LIGHT AND A/S LOAD=316 VA; TOTAL CASE AMPS=3 A; TOTAL CASE WATTAGE=316 W; Timed-Off Defrost Termination Temp=-460 °F
- ON2.5UM-12' - Meat: 5" BF=Yes; ANTI SWEAT APPARENT LOAD=46 VA; ANTI SWEAT HEATER WATTAGE=46 W; BTU ADD FOR LIGHTS=2880; BTU ADD PER SHELF PER FOOT=80; BTUH Conventional=0; BTUH Parallel=0; CONVENTIONAL EVAPORATOR LOAD=12444; DEFROST AMPS=6 A; DRAIN PIPE LENGTH=0"; Defrosts Per Day=0; Discharge Air (°F)=-460 °F; Evaporator (°F)=-460 °F; FAN AND ANTI SWEAT HEATER APPARENT LOAD=83 VA; FAN APPARENT LOAD=37 VA; FAN QUANTITY=4; FAN WATTAGE=18 W; HEIGHT=44 1/16"; High Efficiency Watts=11 W; High Power (Cornice) Watts=0 W; LED LIGHTING AMPS=1 A; LED LIGHTING BTU ADD PER ROW=36; LED LIGHTING WATTAGE=108 W; LENGTH=144"; LENGTH FOR BTU=12; LIGHT AMPS=2 A; LIGHTING APPARENT LOAD=252 VA; LIGHTING WATTAGE=252 VA; Lights Per Row=0; Number of Fans=1; PARALLEL EVAPORATOR LOAD=11748; REF PIPE LENGTH=28 5/8"; REF PLANE LEFT RIGHT=72"; SHELF LIGHT ROWS=3; SHELVE 2=Yes; SHELVE 3=Yes; SHELVE LENGTH=48"; Standard Power Watts=0 W; T8 LIGHTING AMPS=2 A; T8 LIGHTING AMPS PER ROW=1 A; T8 LIGHTING BTU ADD PER ROW=80; T8 LIGHTING WATTAGE=252 W; TOTAL APPARENT FAN-LIGHT AND A/S LOAD=316 VA; TOTAL CASE AMPS=3 A; TOTAL CASE WATTAGE=316 W; Timed-Off Defrost Termination Temp=-460 °F
- ON2.5UM-08' Cut Produce Extended: 5" BF=Yes; ANTI SWEAT APPARENT LOAD=24 VA; ANTI SWEAT HEATER WATTAGE=24 W; BTU ADD FOR LIGHTS=720; BTU ADD PER SHELF PER FOOT=60; BTUH Conventional=0; BTUH Parallel=0; CONVENTIONAL EVAPORATOR LOAD=5502; DEFROST AMPS=3 A; DRAIN PIPE LENGTH=0"; Defrosts Per Day=0; Discharge Air (°F)=-460 °F; Evaporator (°F)=-460 °F; FAN AND ANTI SWEAT HEATER APPARENT LOAD=42 VA; FAN APPARENT LOAD=18 VA; FAN QUANTITY=2; FAN WATTAGE=9 W; HEIGHT=44 1/16"; High Efficiency Watts=11 W; High Power (Cornice) Watts=0 W; LED LIGHTING AMPS=0 A; LED LIGHTING BTU ADD PER ROW=27; LED LIGHTING WATTAGE=34 W; LENGTH=72"; LENGTH FOR BTU=6; LIGHT AMPS=1 A; LIGHTING APPARENT LOAD=89 VA; LIGHTING WATTAGE=89 VA; Lights Per Row=0; Number of Fans=1; PARALLEL EVAPORATOR LOAD=5154; REF PIPE LENGTH=28 5/8"; REF PLANE LEFT RIGHT=36"; SHELF LIGHT ROWS=2; SHELVE 2=No; SHELVE 3=Yes; SHELVE LENGTH=36"; Standard Power Watts=0 W; T8 LIGHTING AMPS=1 A; T8 LIGHTING AMPS PER ROW=0 A; T8 LIGHTING BTU ADD PER ROW=60; T8 LIGHTING WATTAGE=89 W; TOTAL APPARENT FAN-LIGHT AND A/S LOAD=122 VA; TOTAL CASE AMPS=1 A; TOTAL CASE WATTAGE=122 W; Timed-Off Defrost Termination Temp=-460 °F
- ON2.5UM-08' - Meat -  Extended: 5" BF=Yes; ANTI SWEAT APPARENT LOAD=24 VA; ANTI SWEAT HEATER WATTAGE=24 W; BTU ADD FOR LIGHTS=720; BTU ADD PER SHELF PER FOOT=60; BTUH Conventional=0; BTUH Parallel=0; CONVENTIONAL EVAPORATOR LOAD=5502; DEFROST AMPS=3 A; DRAIN PIPE LENGTH=0"; Defrosts Per Day=0; Discharge Air (°F)=-460 °F; Evaporator (°F)=-460 °F; FAN AND ANTI SWEAT HEATER APPARENT LOAD=42 VA; FAN APPARENT LOAD=18 VA; FAN QUANTITY=2; FAN WATTAGE=9 W; HEIGHT=44 1/16"; High Efficiency Watts=11 W; High Power (Cornice) Watts=0 W; LED LIGHTING AMPS=0 A; LED LIGHTING BTU ADD PER ROW=27; LED LIGHTING WATTAGE=34 W; LENGTH=72"; LENGTH FOR BTU=6; LIGHT AMPS=1 A; LIGHTING APPARENT LOAD=89 VA; LIGHTING WATTAGE=89 VA; Lights Per Row=0; Number of Fans=1; PARALLEL EVAPORATOR LOAD=5154; REF PIPE LENGTH=28 5/8"; REF PLANE LEFT RIGHT=36"; SHELF LIGHT ROWS=2; SHELVE 2=No; SHELVE 3=Yes; SHELVE LENGTH=36"; Standard Power Watts=0 W; T8 LIGHTING AMPS=1 A; T8 LIGHTING AMPS PER ROW=0 A; T8 LIGHTING BTU ADD PER ROW=60; T8 LIGHTING WATTAGE=89 W; TOTAL APPARENT FAN-LIGHT AND A/S LOAD=122 VA; TOTAL CASE AMPS=1 A; TOTAL CASE WATTAGE=122 W; Timed-Off Defrost Termination Temp=-460 °F
- ON2.5UM-08' - Meat: 5" BF=Yes; ANTI SWEAT APPARENT LOAD=24 VA; ANTI SWEAT HEATER WATTAGE=24 W; BTU ADD FOR LIGHTS=720; BTU ADD PER SHELF PER FOOT=60; BTUH Conventional=0; BTUH Parallel=0; CONVENTIONAL EVAPORATOR LOAD=5502; DEFROST AMPS=3 A; DRAIN PIPE LENGTH=0"; Defrosts Per Day=0; Discharge Air (°F)=-460 °F; Evaporator (°F)=-460 °F; FAN AND ANTI SWEAT HEATER APPARENT LOAD=42 VA; FAN APPARENT LOAD=18 VA; FAN QUANTITY=2; FAN WATTAGE=9 W; HEIGHT=44 1/16"; High Efficiency Watts=11 W; High Power (Cornice) Watts=0 W; LED LIGHTING AMPS=0 A; LED LIGHTING BTU ADD PER ROW=27; LED LIGHTING WATTAGE=34 W; LENGTH=72"; LENGTH FOR BTU=6; LIGHT AMPS=1 A; LIGHTING APPARENT LOAD=89 VA; LIGHTING WATTAGE=89 VA; Lights Per Row=0; Number of Fans=1; PARALLEL EVAPORATOR LOAD=5154; REF PIPE LENGTH=28 5/8"; REF PLANE LEFT RIGHT=36"; SHELF LIGHT ROWS=2; SHELVE 2=No; SHELVE 3=Yes; SHELVE LENGTH=36"; Standard Power Watts=0 W; T8 LIGHTING AMPS=1 A; T8 LIGHTING AMPS PER ROW=0 A; T8 LIGHTING BTU ADD PER ROW=60; T8 LIGHTING WATTAGE=89 W; TOTAL APPARENT FAN-LIGHT AND A/S LOAD=122 VA; TOTAL CASE AMPS=1 A; TOTAL CASE WATTAGE=122 W; Timed-Off Defrost Termination Temp=-460 °F
- ON2.5UM-06' Cut Produce - Extended: 5" BF=Yes; ANTI SWEAT APPARENT LOAD=24 VA; ANTI SWEAT HEATER WATTAGE=24 W; BTU ADD FOR LIGHTS=720; BTU ADD PER SHELF PER FOOT=60; BTUH Conventional=0; BTUH Parallel=0; CONVENTIONAL EVAPORATOR LOAD=5502; DEFROST AMPS=3 A; DRAIN PIPE LENGTH=0"; Defrosts Per Day=0; Discharge Air (°F)=-460 °F; Evaporator (°F)=-460 °F; FAN AND ANTI SWEAT HEATER APPARENT LOAD=42 VA; FAN APPARENT LOAD=18 VA; FAN QUANTITY=2; FAN WATTAGE=9 W; HEIGHT=44 1/16"; High Efficiency Watts=11 W; High Power (Cornice) Watts=0 W; LED LIGHTING AMPS=0 A; LED LIGHTING BTU ADD PER ROW=27; LED LIGHTING WATTAGE=34 W; LENGTH=72"; LENGTH FOR BTU=6; LIGHT AMPS=1 A; LIGHTING APPARENT LOAD=89 VA; LIGHTING WATTAGE=89 VA; Lights Per Row=0; Number of Fans=1; PARALLEL EVAPORATOR LOAD=5154; REF PIPE LENGTH=28 5/8"; REF PLANE LEFT RIGHT=36"; SHELF LIGHT ROWS=2; SHELVE 2=No; SHELVE 3=Yes; SHELVE LENGTH=36"; Standard Power Watts=0 W; T8 LIGHTING AMPS=1 A; T8 LIGHTING AMPS PER ROW=0 A; T8 LIGHTING BTU ADD PER ROW=60; T8 LIGHTING WATTAGE=89 W; TOTAL APPARENT FAN-LIGHT AND A/S LOAD=122 VA; TOTAL CASE AMPS=1 A; TOTAL CASE WATTAGE=122 W; Timed-Off Defrost Termination Temp=-460 °F
- ON2.5UM-06' Meat - Extended: 5" BF=Yes; ANTI SWEAT APPARENT LOAD=24 VA; ANTI SWEAT HEATER WATTAGE=24 W; BTU ADD FOR LIGHTS=720; BTU ADD PER SHELF PER FOOT=60; BTUH Conventional=0; BTUH Parallel=0; CONVENTIONAL EVAPORATOR LOAD=5502; DEFROST AMPS=3 A; DRAIN PIPE LENGTH=0"; Defrosts Per Day=0; Discharge Air (°F)=-460 °F; Evaporator (°F)=-460 °F; FAN AND ANTI SWEAT HEATER APPARENT LOAD=42 VA; FAN APPARENT LOAD=18 VA; FAN QUANTITY=2; FAN WATTAGE=9 W; HEIGHT=44 1/16"; High Efficiency Watts=11 W; High Power (Cornice) Watts=0 W; LED LIGHTING AMPS=0 A; LED LIGHTING BTU ADD PER ROW=27; LED LIGHTING WATTAGE=34 W; LENGTH=72"; LENGTH FOR BTU=6; LIGHT AMPS=1 A; LIGHTING APPARENT LOAD=89 VA; LIGHTING WATTAGE=89 VA; Lights Per Row=0; Number of Fans=1; PARALLEL EVAPORATOR LOAD=5154; REF PIPE LENGTH=28 5/8"; REF PLANE LEFT RIGHT=36"; SHELF LIGHT ROWS=2; SHELVE 2=No; SHELVE 3=Yes; SHELVE LENGTH=36"; Standard Power Watts=0 W; T8 LIGHTING AMPS=1 A; T8 LIGHTING AMPS PER ROW=0 A; T8 LIGHTING BTU ADD PER ROW=60; T8 LIGHTING WATTAGE=89 W; TOTAL APPARENT FAN-LIGHT AND A/S LOAD=122 VA; TOTAL CASE AMPS=1 A; TOTAL CASE WATTAGE=122 W; Timed-Off Defrost Termination Temp=-460 °F
- ON2.5UM-06' Meat: 5" BF=Yes; ANTI SWEAT APPARENT LOAD=24 VA; ANTI SWEAT HEATER WATTAGE=24 W; BTU ADD FOR LIGHTS=720; BTU ADD PER SHELF PER FOOT=60; BTUH Conventional=0; BTUH Parallel=0; CONVENTIONAL EVAPORATOR LOAD=5502; DEFROST AMPS=3 A; DRAIN PIPE LENGTH=0"; Defrosts Per Day=0; Discharge Air (°F)=-460 °F; Evaporator (°F)=-460 °F; FAN AND ANTI SWEAT HEATER APPARENT LOAD=42 VA; FAN APPARENT LOAD=18 VA; FAN QUANTITY=2; FAN WATTAGE=9 W; HEIGHT=44 1/8"; High Efficiency Watts=11 W; High Power (Cornice) Watts=0 W; LED LIGHTING AMPS=0 A; LED LIGHTING BTU ADD PER ROW=27; LED LIGHTING WATTAGE=34 W; LENGTH=72"; LENGTH FOR BTU=6; LIGHT AMPS=1 A; LIGHTING APPARENT LOAD=89 VA; LIGHTING WATTAGE=89 VA; Lights Per Row=0; Number of Fans=1; PARALLEL EVAPORATOR LOAD=5154; REF PIPE LENGTH=28 5/8"; REF PLANE LEFT RIGHT=36"; SHELF LIGHT ROWS=2; SHELVE 2=No; SHELVE 3=Yes; SHELVE LENGTH=36"; Standard Power Watts=0 W; T8 LIGHTING AMPS=1 A; T8 LIGHTING AMPS PER ROW=0 A; T8 LIGHTING BTU ADD PER ROW=60; T8 LIGHTING WATTAGE=89 W; TOTAL APPARENT FAN-LIGHT AND A/S LOAD=122 VA; TOTAL CASE AMPS=1 A; TOTAL CASE WATTAGE=122 W; Timed-Off Defrost Termination Temp=-460 °F
- ON2.5UM-4'-5"BF: 5" BF=No; ANTI SWEAT APPARENT LOAD=17 VA; ANTI SWEAT HEATER WATTAGE=17 W; BTU ADD FOR LIGHTS=320; BTU ADD PER SHELF PER FOOT=80; BTUH Conventional=0; BTUH Parallel=0; CONVENTIONAL EVAPORATOR LOAD=3508; DEFROST AMPS=2 A; DRAIN PIPE LENGTH=12"; Defrosts Per Day=0; Discharge Air (°F)=-460 °F; Evaporator (°F)=-460 °F; FAN AND ANTI SWEAT HEATER APPARENT LOAD=35 VA; FAN APPARENT LOAD=18 VA; FAN QUANTITY=2; FAN WATTAGE=9 W; HEIGHT=44 1/16"; High Efficiency Watts=11 W; High Power (Cornice) Watts=0 W; LED LIGHTING AMPS=0 A; LED LIGHTING BTU ADD PER ROW=36; LED LIGHTING WATTAGE=12 W; LENGTH=48"; LENGTH FOR BTU=4; LIGHT AMPS=0 A; LIGHTING APPARENT LOAD=28 VA; LIGHTING WATTAGE=28 VA; Lights Per Row=0; Number of Fans=1; PARALLEL EVAPORATOR LOAD=3276; REF PIPE LENGTH=22 9/16"; REF PLANE LEFT RIGHT=24"; SHELF LIGHT ROWS=1; SHELVE 2=No; SHELVE 3=No; SHELVE LENGTH=48"; Standard Power Watts=0 W; T8 LIGHTING AMPS=0 A; T8 LIGHTING AMPS PER ROW=0 A; T8 LIGHTING BTU ADD PER ROW=80; T8 LIGHTING WATTAGE=28 W; TOTAL APPARENT FAN-LIGHT AND A/S LOAD=54 VA; TOTAL CASE AMPS=1 A; TOTAL CASE WATTAGE=54 W; Timed-Off Defrost Termination Temp=-460 °F
- ON2.5UM-6'-5"BF: 5" BF=Yes; ANTI SWEAT APPARENT LOAD=24 VA; ANTI SWEAT HEATER WATTAGE=24 W; BTU ADD FOR LIGHTS=720; BTU ADD PER SHELF PER FOOT=60; BTUH Conventional=0; BTUH Parallel=0; CONVENTIONAL EVAPORATOR LOAD=5502; DEFROST AMPS=3 A; DRAIN PIPE LENGTH=0"; Defrosts Per Day=0; Discharge Air (°F)=-460 °F; Evaporator (°F)=-460 °F; FAN AND ANTI SWEAT HEATER APPARENT LOAD=42 VA; FAN APPARENT LOAD=18 VA; FAN QUANTITY=2; FAN WATTAGE=9 W; HEIGHT=44 1/16"; High Efficiency Watts=11 W; High Power (Cornice) Watts=0 W; LED LIGHTING AMPS=0 A; LED LIGHTING BTU ADD PER ROW=27; LED LIGHTING WATTAGE=34 W; LENGTH=72"; LENGTH FOR BTU=6; LIGHT AMPS=1 A; LIGHTING APPARENT LOAD=89 VA; LIGHTING WATTAGE=89 VA; Lights Per Row=0; Number of Fans=1; PARALLEL EVAPORATOR LOAD=5154; REF PIPE LENGTH=28 5/8"; REF PLANE LEFT RIGHT=36"; SHELF LIGHT ROWS=2; SHELVE 2=No; SHELVE 3=Yes; SHELVE LENGTH=36"; Standard Power Watts=0 W; T8 LIGHTING AMPS=1 A; T8 LIGHTING AMPS PER ROW=0 A; T8 LIGHTING BTU ADD PER ROW=60; T8 LIGHTING WATTAGE=89 W; TOTAL APPARENT FAN-LIGHT AND A/S LOAD=122 VA; TOTAL CASE AMPS=1 A; TOTAL CASE WATTAGE=122 W; Timed-Off Defrost Termination Temp=-460 °F
- ON2.5UM-8'-5"BF: 5" BF=Yes; ANTI SWEAT APPARENT LOAD=30 VA; ANTI SWEAT HEATER WATTAGE=30 W; BTU ADD FOR LIGHTS=1280; BTU ADD PER SHELF PER FOOT=80; BTUH Conventional=0; BTUH Parallel=0; CONVENTIONAL EVAPORATOR LOAD=7656; DEFROST AMPS=4 A; DRAIN PIPE LENGTH=0"; Defrosts Per Day=0; Discharge Air (°F)=-460 °F; Evaporator (°F)=-460 °F; FAN AND ANTI SWEAT HEATER APPARENT LOAD=58 VA; FAN APPARENT LOAD=28 VA; FAN QUANTITY=3; FAN WATTAGE=14 W; HEIGHT=44 1/16"; High Efficiency Watts=11 W; High Power (Cornice) Watts=0 W; LED LIGHTING AMPS=0 A; LED LIGHTING BTU ADD PER ROW=36; LED LIGHTING WATTAGE=48 W; LENGTH=96"; LENGTH FOR BTU=8; LIGHT AMPS=1 A; LIGHTING APPARENT LOAD=113 VA; LIGHTING WATTAGE=113 VA; Lights Per Row=0; Number of Fans=1; PARALLEL EVAPORATOR LOAD=7192; REF PIPE LENGTH=28 5/8"; REF PLANE LEFT RIGHT=48"; SHELF LIGHT ROWS=2; SHELVE 2=No; SHELVE 3=Yes; SHELVE LENGTH=48"; Standard Power Watts=0 W; T8 LIGHTING AMPS=1 A; T8 LIGHTING AMPS PER ROW=0 A; T8 LIGHTING BTU ADD PER ROW=80; T8 LIGHTING WATTAGE=113 W; TOTAL APPARENT FAN-LIGHT AND A/S LOAD=157 VA; TOTAL CASE AMPS=1 A; TOTAL CASE WATTAGE=157 W; Timed-Off Defrost Termination Temp=-460 °F
- ON2.5UM-12'-5"BF: 5" BF=Yes; ANTI SWEAT APPARENT LOAD=46 VA; ANTI SWEAT HEATER WATTAGE=46 W; BTU ADD FOR LIGHTS=2880; BTU ADD PER SHELF PER FOOT=80; BTUH Conventional=0; BTUH Parallel=0; CONVENTIONAL EVAPORATOR LOAD=12444; DEFROST AMPS=6 A; DRAIN PIPE LENGTH=0"; Defrosts Per Day=0; Discharge Air (°F)=-460 °F; Evaporator (°F)=-460 °F; FAN AND ANTI SWEAT HEATER APPARENT LOAD=83 VA; FAN APPARENT LOAD=37 VA; FAN QUANTITY=4; FAN WATTAGE=18 W; HEIGHT=44 1/16"; High Efficiency Watts=11 W; High Power (Cornice) Watts=0 W; LED LIGHTING AMPS=1 A; LED LIGHTING BTU ADD PER ROW=36; LED LIGHTING WATTAGE=108 W; LENGTH=144"; LENGTH FOR BTU=12; LIGHT AMPS=2 A; LIGHTING APPARENT LOAD=252 VA; LIGHTING WATTAGE=252 VA; Lights Per Row=0; Number of Fans=1; PARALLEL EVAPORATOR LOAD=11748; REF PIPE LENGTH=28 5/8"; REF PLANE LEFT RIGHT=72"; SHELF LIGHT ROWS=3; SHELVE 2=Yes; SHELVE 3=Yes; SHELVE LENGTH=48"; Standard Power Watts=0 W; T8 LIGHTING AMPS=2 A; T8 LIGHTING AMPS PER ROW=1 A; T8 LIGHTING BTU ADD PER ROW=80; T8 LIGHTING WATTAGE=252 W; TOTAL APPARENT FAN-LIGHT AND A/S LOAD=316 VA; TOTAL CASE AMPS=3 A; TOTAL CASE WATTAGE=316 W; Timed-Off Defrost Termination Temp=-460 °F

## geometry (parser evidence)
native form markers: Blend x2, Sweep x2
no freeform markers — native parametric forms only
